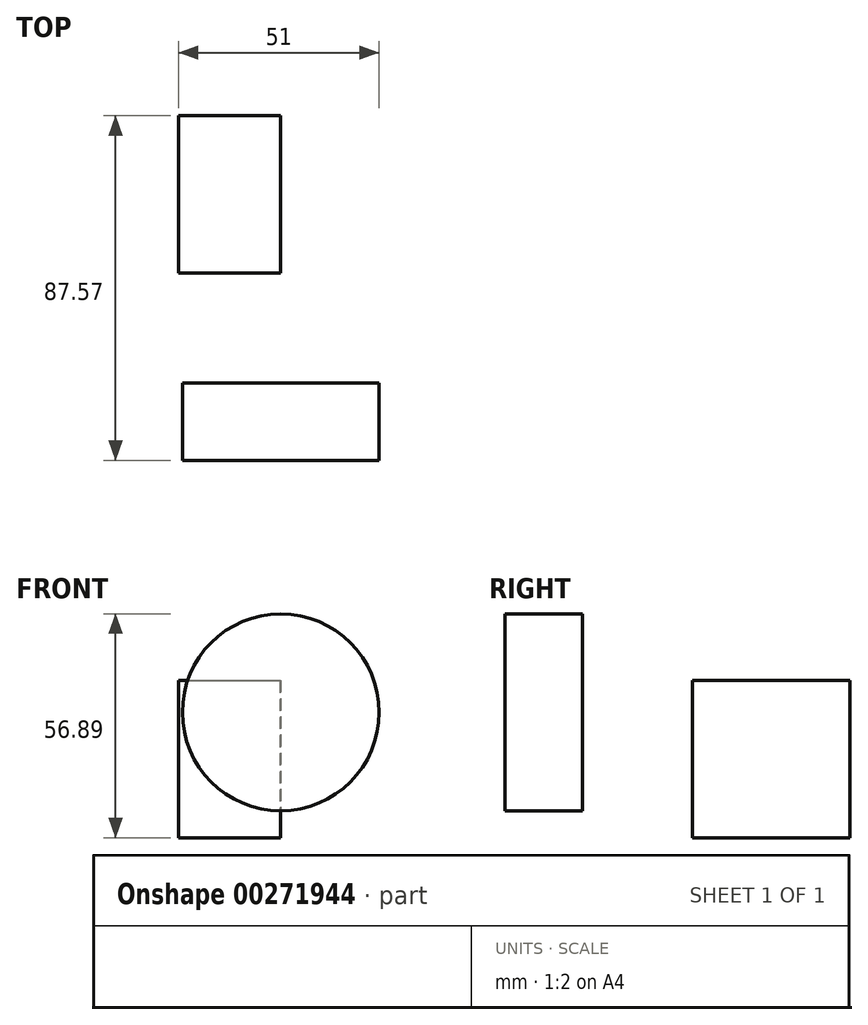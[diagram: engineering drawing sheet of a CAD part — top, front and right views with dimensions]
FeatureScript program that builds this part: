
annotation { "Feature Type Name" : "Feature", "Feature Type Description" : "" }
export const myFeature = defineFeature(function(context is Context, id is Id, definition is map)
    precondition{}
    {
        {
            var Q0;
            Q0=qCreatedBy(makeId("Right.planeOp"),FACE);
            var sketch = newSketch(context, id + "F0", { "sketchPlane" : qUnion([Q0])});
            skLineSegment(sketch, "E0", {"start": v(0, 0) * mm, "end": v(40, 0) * mm});
            skLineSegment(sketch, "E1", {"start": v(40, 0) * mm, "end": v(40, 40) * mm});
            skLineSegment(sketch, "E2", {"start": v(40, 40) * mm, "end": v(0, 40) * mm});
            skLineSegment(sketch, "E3", {"start": v(0, 40) * mm, "end": v(0, 0) * mm});
            skSolve(sketch);
        }
        {
            var Q0;
            Q0=makeQuery(id+"F0.imprint","IMPRINT",FACE,{"disambiguationData":[TD([[makeQuery(id+"F0.imprint","IMPRINT",EDGE,{"derivedFrom":sQuery(id+"F0.wireOp",EDGE,"E0")}),1.0]])]});
            extrude(context, id + "F1", {"entities" : qUnion([Q0]), "oppositeDirection" : true, "depth" : 26 * mm});
        }
        {
            var Q0;
            Q0=qCreatedBy(makeId("Right.planeOp"),FACE);
            var sketch = newSketch(context, id + "F2", { "sketchPlane" : qUnion([Q0])});
            skLineSegment(sketch, "E4", {"start": v(-47.57, 6.89) * mm, "end": v(-47.57, 31.89) * mm});
            skLineSegment(sketch, "E5", {"start": v(-47.57, 31.89) * mm, "end": v(-27.95, 31.89) * mm});
            skLineSegment(sketch, "E6", {"start": v(-27.95, 31.89) * mm, "end": v(-27.95, 6.89) * mm});
            skLineSegment(sketch, "E7", {"start": v(-47.57, 6.89) * mm, "end": v(-27.95, 6.89) * mm});
            skLineSegment(sketch, "E8", {"start": v(-47.57, 31.89) * mm, "end": v(-75.26, 31.89) * mm, "construction": true});
            skSolve(sketch);
        }
        {
            var Q0;
            Q0 = qSketchRegion(id + "F2", true);
            var Q1;
            Q1=sQuery(id+"F2.wireOp",EDGE,"E8");
            revolve(context, id + "F3", {"entities" : qUnion([Q0]), "axis" : qUnion([Q1]), "revolveType" : RevolveType.FULL});
        }
    });
